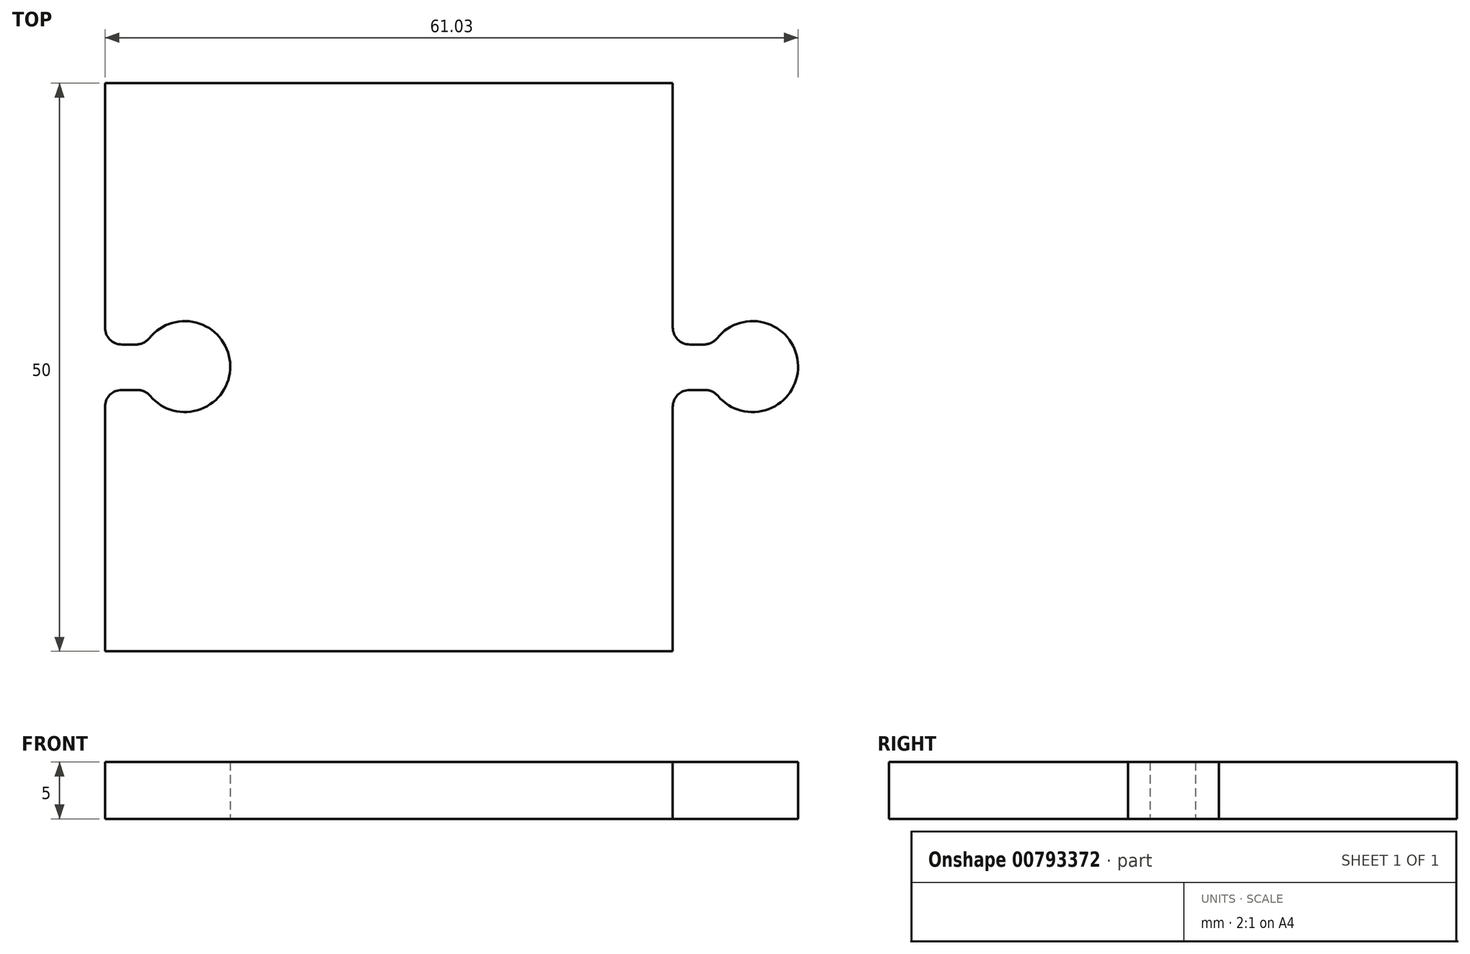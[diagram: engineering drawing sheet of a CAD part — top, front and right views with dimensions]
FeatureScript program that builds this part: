
annotation { "Feature Type Name" : "Feature", "Feature Type Description" : "" }
export const myFeature = defineFeature(function(context is Context, id is Id, definition is map)
    precondition{}
    {
        {
            var Q0;
            Q0=qCreatedBy(makeId("Top.planeOp"),FACE);
            var sketch = newSketch(context, id + "F0", { "sketchPlane" : qUnion([Q0])});
            skLineSegment(sketch, "E0.bottom", {"start": v(22.8, -24.61) * mm, "end": v(-27.2, -24.61) * mm});
            skLineSegment(sketch, "E0.top", {"start": v(22.8, 25.39) * mm, "end": v(-27.2, 25.39) * mm});
            skLineSegment(sketch, "E0.left", {"start": v(22.8, -24.61) * mm, "end": v(22.8, -3.11) * mm});
            skLineSegment(sketch, "E0.right", {"start": v(-27.2, -24.61) * mm, "end": v(-27.2, -3.11) * mm});
            skLineSegment(sketch, "E1", {"start": v(-25.7, -1.61) * mm, "end": v(-24.36, -1.61) * mm});
            skLineSegment(sketch, "E2", {"start": v(-27.2, 25.39) * mm, "end": v(-27.2, 3.89) * mm});
            skLineSegment(sketch, "E3", {"start": v(-25.7, 2.39) * mm, "end": v(-24.46, 2.39) * mm});
            skArc(sketch, "E4", {"start": v(-23.22, -2.14) * mm, "mid": v(-16.17, 0.5) * mm, "end": v(-23.29, 2.95) * mm});
            skPoint(sketch, "E5.end.orphan", {"position": v(-27.2, 0.39) * mm});
            skLineSegment(sketch, "E6.trimOffspring", {"start": v(-27.2, 3.89) * mm, "end": v(-27.2, 25.39) * mm});
            skPoint(sketch, "E7.visualSharp", {"position": v(-27.2, 2.39) * mm});
            skArc(sketch, "E7.filletArc", {"start": v(-27.2, 3.89) * mm, "mid": v(-26.76, 2.83) * mm, "end": v(-25.7, 2.39) * mm});
            skPoint(sketch, "E8.visualSharp", {"position": v(-27.2, -1.61) * mm});
            skArc(sketch, "E8.filletArc", {"start": v(-25.7, -1.61) * mm, "mid": v(-26.76, -2.05) * mm, "end": v(-27.2, -3.11) * mm});
            skPoint(sketch, "E9.visualSharp", {"position": v(-23.66, 2.39) * mm});
            skArc(sketch, "E9.filletArc", {"start": v(-24.46, 2.39) * mm, "mid": v(-23.8, 2.54) * mm, "end": v(-23.29, 2.95) * mm});
            skPoint(sketch, "E10.visualSharp", {"position": v(-23.6, -1.61) * mm});
            skArc(sketch, "E10.filletArc", {"start": v(-23.22, -2.14) * mm, "mid": v(-23.73, -1.75) * mm, "end": v(-24.36, -1.61) * mm});
            skLineSegment(sketch, "E11", {"start": v(-20.17, 0.45) * mm, "end": v(-27.2, 0.39) * mm});
            skPoint(sketch, "E12.orphan", {"position": v(22.8, 0.45) * mm});
            skLineSegment(sketch, "E13", {"start": v(22.8, 25.39) * mm, "end": v(22.8, 3.89) * mm});
            skLineSegment(sketch, "E14", {"start": v(24.3, -1.61) * mm, "end": v(25.63, -1.61) * mm});
            skLineSegment(sketch, "E15", {"start": v(24.3, 2.39) * mm, "end": v(25.54, 2.39) * mm});
            skArc(sketch, "E16", {"start": v(26.78, -2.14) * mm, "mid": v(33.83, 0.5) * mm, "end": v(26.7, 2.95) * mm});
            skPoint(sketch, "E17.visualSharp", {"position": v(22.8, 2.39) * mm});
            skArc(sketch, "E17.filletArc", {"start": v(22.8, 3.89) * mm, "mid": v(23.24, 2.83) * mm, "end": v(24.3, 2.39) * mm});
            skPoint(sketch, "E18.newPointA", {"position": v(22.8, -1.61) * mm});
            skArc(sketch, "E18.filletArc", {"start": v(24.3, -1.61) * mm, "mid": v(23.24, -2.05) * mm, "end": v(22.8, -3.11) * mm});
            skPoint(sketch, "E19.orphan", {"position": v(33.26, 2.39) * mm});
            skLineSegment(sketch, "E20.trimOffspring", {"start": v(33.26, -1.61) * mm, "end": v(33.26, -1.61) * mm});
            skPoint(sketch, "E21.visualSharp", {"position": v(26.33, 2.39) * mm});
            skArc(sketch, "E21.filletArc", {"start": v(25.54, 2.39) * mm, "mid": v(26.19, 2.54) * mm, "end": v(26.7, 2.95) * mm});
            skPoint(sketch, "E22.visualSharp", {"position": v(26.4, -1.61) * mm});
            skArc(sketch, "E22.filletArc", {"start": v(26.78, -2.14) * mm, "mid": v(26.26, -1.75) * mm, "end": v(25.63, -1.61) * mm});
            skSolve(sketch);
        }
        {
            var Q0;
            Q0 = qSketchRegion(id + "F0", true);
            extrude(context, id + "F1", {"entities" : qUnion([Q0]), "depth" : 5 * mm, "offsetDistance" : 25 * mm});
        }
    });
